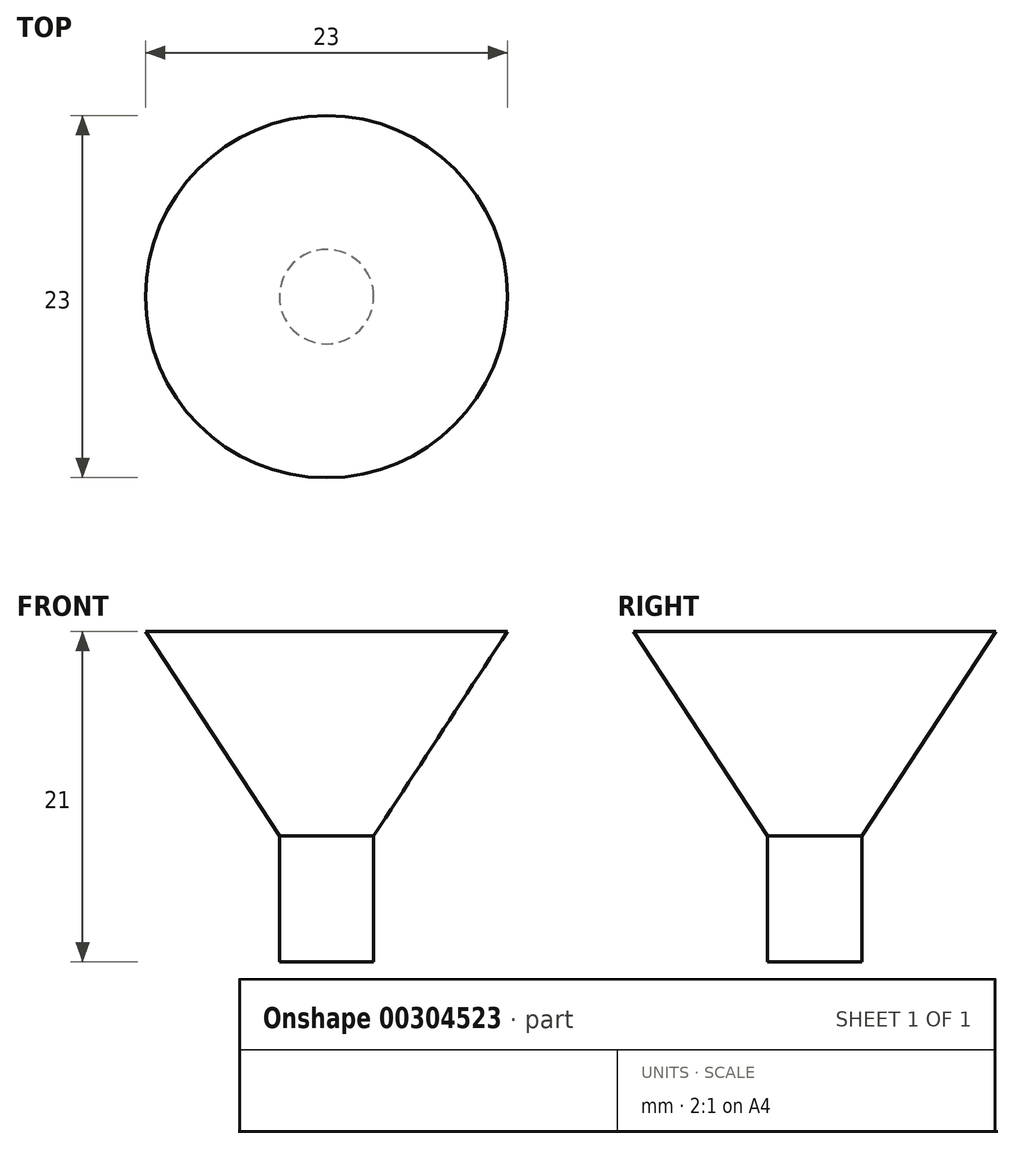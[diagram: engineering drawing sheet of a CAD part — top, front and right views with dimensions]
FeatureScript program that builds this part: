
annotation { "Feature Type Name" : "Feature", "Feature Type Description" : "" }
export const myFeature = defineFeature(function(context is Context, id is Id, definition is map)
    precondition{}
    {
        {
            var Q0;
            Q0=qCreatedBy(makeId("Top.planeOp"),FACE);
            var sketch = newSketch(context, id + "F0", { "sketchPlane" : qUnion([Q0])});
            skCircle(sketch, "E0", {"center": v(0, 0) * mm, "radius": 3 * mm});
            skSolve(sketch);
        }
        {
            var Q0;
            Q0=makeQuery(id+"F0.imprint","IMPRINT",FACE,{"disambiguationData":[TD([[makeQuery(id+"F0.imprint","IMPRINT",EDGE,{"derivedFrom":sQuery(id+"F0.wireOp",EDGE,"E0")}),1.0]])]});
            cPlane(context, id + "F1", {"entities" : qUnion([Q0]), "cplaneType" : CPlaneType.OFFSET, "offset" : 8 * mm, "width" : 150 * mm, "height" : 150 * mm});
        }
        {
            var Q0;
            Q0=makeQuery(id+"F0.imprint","IMPRINT",FACE,{"disambiguationData":[TD([[makeQuery(id+"F0.imprint","IMPRINT",EDGE,{"derivedFrom":sQuery(id+"F0.wireOp",EDGE,"E0")}),1.0]])]});
            extrude(context, id + "F2", {"entities" : qUnion([Q0]), "depth" : 8 * mm});
        }
        {
            var Q0;
            Q0=qCreatedBy(id+"F1.planeOp",FACE);
            var sketch = newSketch(context, id + "F3", { "sketchPlane" : qUnion([Q0])});
            skCircle(sketch, "E1", {"center": v(0, 0) * mm, "radius": 3 * mm});
            skSolve(sketch);
        }
        {
            var Q0;
            Q0=qCreatedBy(id+"F1.planeOp",FACE);
            cPlane(context, id + "F4", {"entities" : qUnion([Q0]), "cplaneType" : CPlaneType.OFFSET, "offset" : 13 * mm, "width" : 150 * mm, "height" : 150 * mm});
        }
        {
            var Q0;
            Q0=qCreatedBy(id+"F4.planeOp",FACE);
            var sketch = newSketch(context, id + "F5", { "sketchPlane" : qUnion([Q0])});
            skCircle(sketch, "E2", {"center": v(0, 0) * mm, "radius": 11.5 * mm});
            skSolve(sketch);
        }
        {
            var Q1;
            Q1=makeQuery(id+"F3.imprint","IMPRINT",FACE,{"disambiguationData":[TD([[makeQuery(id+"F3.imprint","IMPRINT",EDGE,{"derivedFrom":sQuery(id+"F3.wireOp",EDGE,"E1")}),1.0]])]});
            var Q2;
            Q2=makeQuery(id+"F5.imprint","IMPRINT",FACE,{"disambiguationData":[TD([[makeQuery(id+"F5.imprint","IMPRINT",EDGE,{"derivedFrom":sQuery(id+"F5.wireOp",EDGE,"E2")}),1.0]])]});
            loft(context, id + "F6", {"operationType" : NewBodyOperationType.ADD, "sheetProfilesArray" : [{ "sheetProfileEntities" : qUnion([Q1]) }, { "sheetProfileEntities" : qUnion([Q2]) }]});
        }
    });
